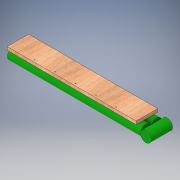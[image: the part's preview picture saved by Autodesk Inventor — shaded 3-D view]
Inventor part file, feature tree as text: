
AUTODESK INVENTOR PART (.ipt)
format: ipt  version: 2018 (Build 220112000, 112)  size: 156,160 bytes
history: native  units: in
note: dims shown in document units (in); Inventor stores cm internally (conversion verified against a paired STEP export)
features: extrude x4, sketch x4
ambient origin geometry x8: Origin, YZ Plane, XZ Plane, XY Plane, X Axis, Y Axis, Z Axis, Center Point
bodies: Solid1 (feature_tree)
feature tree (8):
  extrude  "Extrusion1"  Depth=0.75in
  extrude  "Extrusion2"  Depth=1.25in
  extrude  "Extrusion4"  Depth=1.25in
  extrude  "Extrusion6"  Depth=1.25in
  sketch  "Sketch1"  dims[d0=30.0in d1=0.75in]
  sketch  "Sketch2"  dims[d2=5.0in d3=0.0in d4=1.25in]
  sketch  "Sketch4"  dims[d5=1.25in d6=2.5in]
  sketch  "Sketch5"  dims[d7=31.0in d8=0.0in d13=1.25in d14=5.0in d15=0.0in d16=0.5in d17=5.875in d30=0.2031in d33=4.75in d34=4.75in d35=4.75in d36=4.75in d37=0.75in d38=0.0in]
